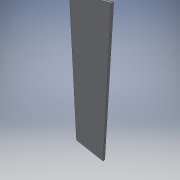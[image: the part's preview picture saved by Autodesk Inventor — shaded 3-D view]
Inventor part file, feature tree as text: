
AUTODESK INVENTOR PART (.ipt)
format: ipt  version: 2016 (Build 200138000, 138)  size: 88,576 bytes
history: native  units: in
note: dims shown in document units (in); Inventor stores cm internally (conversion verified against a paired STEP export)
features: extrude x1, sketch x1
ambient origin geometry x8: Origin, YZ Plane, XZ Plane, XY Plane, X Axis, Y Axis, Z Axis, Center Point
bodies: Solid1 (feature_tree)
feature tree (2):
  extrude  "Extrusion1"  Depth=16.0in
  sketch  "Sketch1"  dims[d0=62.0in d1=16.0in d2=1.0in d3=0.0in]
